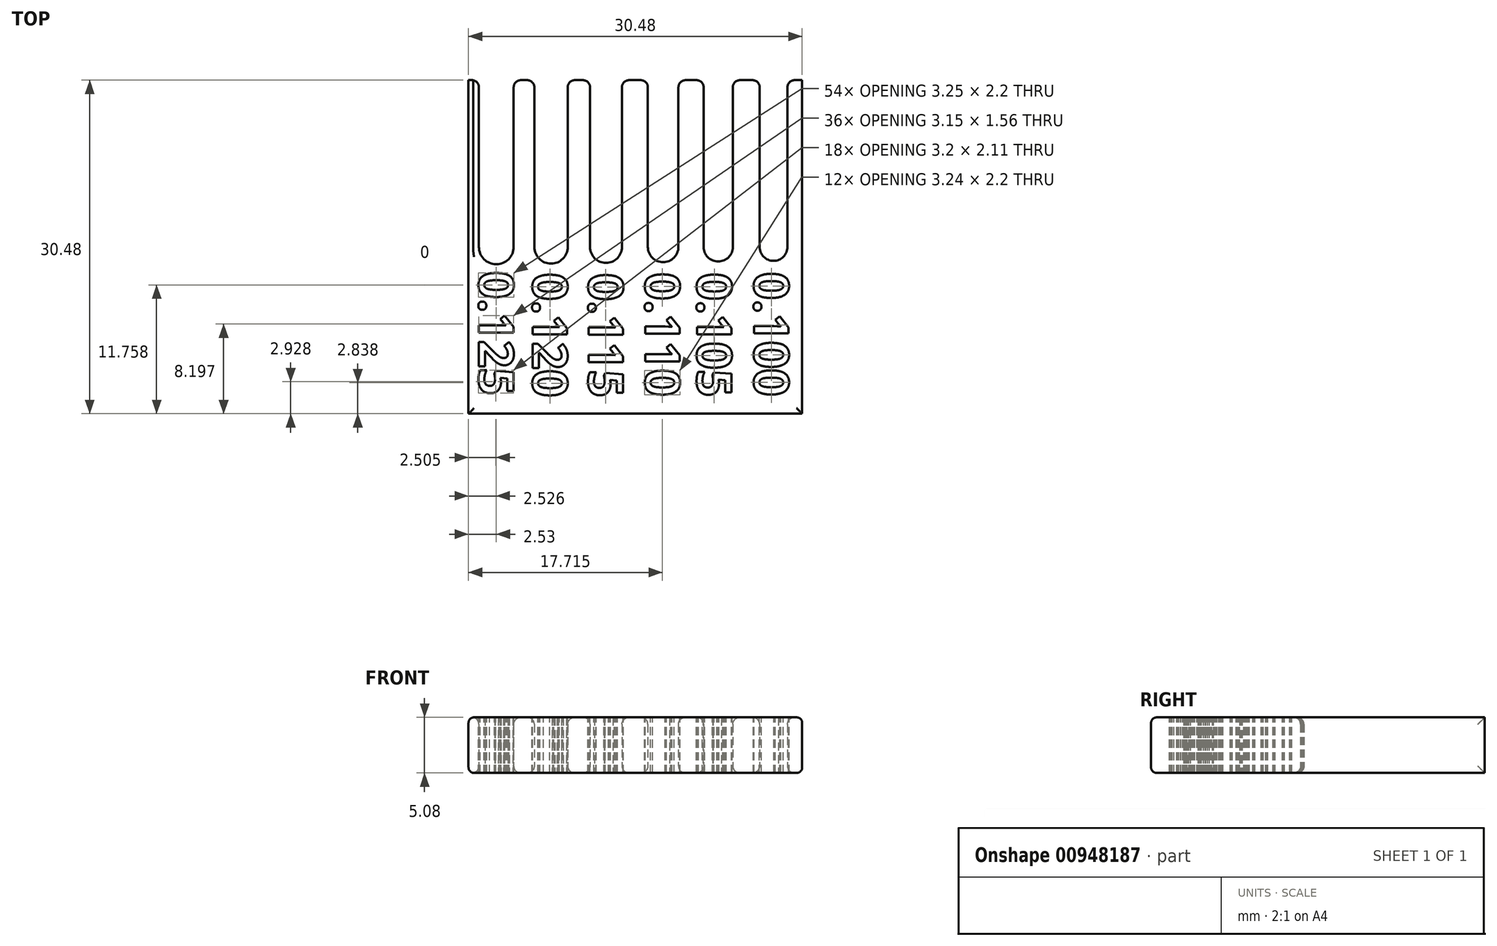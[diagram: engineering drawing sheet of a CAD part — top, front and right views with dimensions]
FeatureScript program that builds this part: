
annotation { "Feature Type Name" : "Feature", "Feature Type Description" : "" }
export const myFeature = defineFeature(function(context is Context, id is Id, definition is map)
    precondition{}
    {
        {
            var Q0;
            Q0=qCreatedBy(makeId("Top.planeOp"),FACE);
            var sketch = newSketch(context, id + "F0", { "sketchPlane" : qUnion([Q0])});
            skLineSegment(sketch, "E0.bottom", {"start": v(2.54, 15.24) * mm, "end": v(-2.54, 15.24) * mm});
            skLineSegment(sketch, "E0.top", {"start": v(2.54, -15.24) * mm, "end": v(-2.54, -15.24) * mm});
            skLineSegment(sketch, "E0.left", {"start": v(2.54, 15.24) * mm, "end": v(2.54, -15.24) * mm});
            skLineSegment(sketch, "E0.right", {"start": v(-2.54, 15.24) * mm, "end": v(-2.54, -15.24) * mm});
            skPoint(sketch, "E0.middle", {"position": v(0, 0) * mm});
            skLineSegment(sketch, "E1", {"start": v(-1.59, 15.24) * mm, "end": v(-1.59, 0) * mm});
            skArc(sketch, "E2", {"start": v(-1.59, 0) * mm, "mid": v(0, -1.59) * mm, "end": v(1.59, 0) * mm});
            skLineSegment(sketch, "E3", {"start": v(1.59, 0) * mm, "end": v(1.59, 15.24) * mm});
            skLineSegment(sketch, "E4.1.0.0", {"start": v(7.62, 15.24) * mm, "end": v(7.62, -15.24) * mm});
            skLineSegment(sketch, "E4.1.0.1", {"start": v(7.62, 15.24) * mm, "end": v(2.54, 15.24) * mm});
            skLineSegment(sketch, "E4.1.0.2", {"start": v(7.62, -15.24) * mm, "end": v(2.54, -15.24) * mm});
            skLineSegment(sketch, "E4.2.0.0", {"start": v(12.7, 15.24) * mm, "end": v(12.7, -15.24) * mm});
            skLineSegment(sketch, "E4.2.0.1", {"start": v(12.7, 15.24) * mm, "end": v(7.62, 15.24) * mm});
            skLineSegment(sketch, "E4.2.0.2", {"start": v(12.7, -15.24) * mm, "end": v(7.62, -15.24) * mm});
            skLineSegment(sketch, "E4.2.0.3", {"start": v(7.62, 15.24) * mm, "end": v(7.62, -15.24) * mm});
            skLineSegment(sketch, "E4.direction1", {"start": v(2.54, -15.24) * mm, "end": v(7.62, -15.24) * mm, "construction": true});
            skPoint(sketch, "E5.middle", {"position": v(5, 0) * mm});
            skLineSegment(sketch, "E6", {"start": v(3.47, 15.24) * mm, "end": v(3.47, 0) * mm});
            skArc(sketch, "E7", {"start": v(3.47, 0) * mm, "mid": v(5, -1.52) * mm, "end": v(6.52, 0) * mm});
            skLineSegment(sketch, "E8", {"start": v(6.52, 0) * mm, "end": v(6.52, 15.24) * mm});
            skPoint(sketch, "E9.middle", {"position": v(10.02, 0) * mm});
            skLineSegment(sketch, "E10", {"start": v(8.56, 15.24) * mm, "end": v(8.56, 0) * mm});
            skArc(sketch, "E11", {"start": v(8.56, 0) * mm, "mid": v(10.02, -1.46) * mm, "end": v(11.48, 0) * mm});
            skLineSegment(sketch, "E12", {"start": v(11.48, 0) * mm, "end": v(11.48, 15.24) * mm});
            skLineSegment(sketch, "E13.bottom", {"start": v(17.78, 15.24) * mm, "end": v(12.7, 15.24) * mm});
            skLineSegment(sketch, "E13.top", {"start": v(17.78, -15.24) * mm, "end": v(12.7, -15.24) * mm});
            skLineSegment(sketch, "E13.left", {"start": v(17.78, 15.24) * mm, "end": v(17.78, -15.24) * mm});
            skPoint(sketch, "E13.middle", {"position": v(15.24, 0) * mm});
            skLineSegment(sketch, "E14", {"start": v(13.84, 15.24) * mm, "end": v(13.84, 0) * mm});
            skArc(sketch, "E15", {"start": v(13.84, 0) * mm, "mid": v(15.24, -1.4) * mm, "end": v(16.64, 0) * mm});
            skLineSegment(sketch, "E16", {"start": v(16.64, 0) * mm, "end": v(16.64, 15.24) * mm});
            skLineSegment(sketch, "E17.1.0.0", {"start": v(22.86, 15.24) * mm, "end": v(22.86, -15.24) * mm});
            skLineSegment(sketch, "E17.1.0.1", {"start": v(22.86, 15.24) * mm, "end": v(17.78, 15.24) * mm});
            skLineSegment(sketch, "E17.1.0.2", {"start": v(22.86, -15.24) * mm, "end": v(17.78, -15.24) * mm});
            skLineSegment(sketch, "E17.2.0.0", {"start": v(27.94, 15.24) * mm, "end": v(27.94, -15.24) * mm});
            skLineSegment(sketch, "E17.2.0.1", {"start": v(27.94, 15.24) * mm, "end": v(22.86, 15.24) * mm});
            skLineSegment(sketch, "E17.2.0.2", {"start": v(27.94, -15.24) * mm, "end": v(22.86, -15.24) * mm});
            skLineSegment(sketch, "E17.2.0.3", {"start": v(22.86, 15.24) * mm, "end": v(22.86, -15.24) * mm});
            skLineSegment(sketch, "E17.direction1", {"start": v(17.78, -15.24) * mm, "end": v(22.86, -15.24) * mm, "construction": true});
            skPoint(sketch, "E18.middle", {"position": v(20.27, 0) * mm});
            skLineSegment(sketch, "E19", {"start": v(18.94, 15.24) * mm, "end": v(18.94, 0) * mm});
            skArc(sketch, "E20", {"start": v(18.94, 0) * mm, "mid": v(20.27, -1.33) * mm, "end": v(21.6, 0) * mm});
            skLineSegment(sketch, "E21", {"start": v(21.6, 0) * mm, "end": v(21.6, 15.24) * mm});
            skPoint(sketch, "E22.middle", {"position": v(25.32, 0) * mm});
            skLineSegment(sketch, "E23", {"start": v(24.05, 15.24) * mm, "end": v(24.05, 0) * mm});
            skArc(sketch, "E24", {"start": v(24.05, 0) * mm, "mid": v(25.32, -1.27) * mm, "end": v(26.6, 0) * mm});
            skLineSegment(sketch, "E25", {"start": v(26.6, 0) * mm, "end": v(26.6, 15.24) * mm});
            skSolve(sketch);
        }
        {
            var Q0;
            Q0=makeQuery(id+"F0.imprint","IMPRINT",FACE,{"disambiguationData":[TD([[makeQuery(id+"F0.imprint","IMPRINT",EDGE,{"derivedFrom":sQuery(id+"F0.wireOp",EDGE,"E0.top")}),-1.0]])]});
            var Q1;
            Q1=makeQuery(id+"F0.imprint","IMPRINT",FACE,{"disambiguationData":[TD([[makeQuery(id+"F0.imprint","IMPRINT",EDGE,{"derivedFrom":sQuery(id+"F0.wireOp",EDGE,"E4.1.0.2")}),-1.0]])]});
            var Q2;
            Q2=makeQuery(id+"F0.imprint","IMPRINT",FACE,{"disambiguationData":[TD([[makeQuery(id+"F0.imprint","IMPRINT",EDGE,{"derivedFrom":sQuery(id+"F0.wireOp",EDGE,"E4.2.0.2")}),-1.0]])]});
            var Q3;
            Q3=makeQuery(id+"F0.imprint","IMPRINT",FACE,{"disambiguationData":[TD([[makeQuery(id+"F0.imprint","IMPRINT",EDGE,{"derivedFrom":sQuery(id+"F0.wireOp",EDGE,"E13.top")}),-1.0]])]});
            var Q4;
            Q4=makeQuery(id+"F0.imprint","IMPRINT",FACE,{"disambiguationData":[TD([[makeQuery(id+"F0.imprint","IMPRINT",EDGE,{"derivedFrom":sQuery(id+"F0.wireOp",EDGE,"E17.1.0.2")}),-1.0]])]});
            var Q5;
            {var subQ3=sQuery(id+"F0.wireOp",EDGE,"E17.2.0.0");Q5=makeQuery(id+"F0.imprint","IMPRINT",FACE,{"disambiguationData":[TD([[makeQuery(id+"F0.imprint","IMPRINT",EDGE,{"derivedFrom":subQ3}),-1.0]])]});}
            extrude(context, id + "F1", {"entities" : qUnion([Q0, Q1, Q2, Q3, Q4, Q5]), "depth" : 5.08 * mm, "offsetDistance" : 25.4 * mm});
        }
        {
            var Q0;
            Q0=makeQuery(id+"F1.opExtrude","CAP_EDGE",EDGE,{"disambiguationData":[OSD([sQuery(id+"F0.wireOp",EDGE,"E2")])],"isStart":false});
            var Q1;
            Q1=makeQuery(id+"F1.opExtrude","CAP_EDGE",EDGE,{"disambiguationData":[OSD([sQuery(id+"F0.wireOp",EDGE,"E7")])],"isStart":false});
            var Q2;
            Q2=makeQuery(id+"F1.opExtrude","CAP_EDGE",EDGE,{"disambiguationData":[OSD([sQuery(id+"F0.wireOp",EDGE,"E11")])],"isStart":false});
            var Q3;
            Q3=makeQuery(id+"F1.opExtrude","CAP_EDGE",EDGE,{"disambiguationData":[OSD([sQuery(id+"F0.wireOp",EDGE,"E15")])],"isStart":false});
            var Q4;
            Q4=makeQuery(id+"F1.opExtrude","CAP_EDGE",EDGE,{"disambiguationData":[OSD([sQuery(id+"F0.wireOp",EDGE,"E20")])],"isStart":false});
            var Q5;
            Q5=makeQuery(id+"F1.opExtrude","CAP_EDGE",EDGE,{"disambiguationData":[OSD([sQuery(id+"F0.wireOp",EDGE,"E24")])],"isStart":false});
            var Q6;
            Q6=makeQuery(id+"F1.opExtrude","CAP_EDGE",EDGE,{"disambiguationData":[OSD([sQuery(id+"F0.wireOp",EDGE,"E24")])],"isStart":true});
            var Q7;
            Q7=makeQuery(id+"F1.opExtrude","CAP_EDGE",EDGE,{"disambiguationData":[OSD([sQuery(id+"F0.wireOp",EDGE,"E20")])],"isStart":true});
            var Q8;
            Q8=makeQuery(id+"F1.opExtrude","CAP_EDGE",EDGE,{"disambiguationData":[OSD([sQuery(id+"F0.wireOp",EDGE,"E15")])],"isStart":true});
            var Q9;
            Q9=makeQuery(id+"F1.opExtrude","CAP_EDGE",EDGE,{"disambiguationData":[OSD([sQuery(id+"F0.wireOp",EDGE,"E11")])],"isStart":true});
            var Q10;
            Q10=makeQuery(id+"F1.opExtrude","CAP_EDGE",EDGE,{"disambiguationData":[OSD([sQuery(id+"F0.wireOp",EDGE,"E7")])],"isStart":true});
            var Q11;
            Q11=makeQuery(id+"F1.opExtrude","CAP_EDGE",EDGE,{"disambiguationData":[OSD([sQuery(id+"F0.wireOp",EDGE,"E2")])],"isStart":true});
            var Q12;
            Q12=makeQuery(id+"F1.opExtrude","SWEPT_EDGE",EDGE,{"disambiguationData":[OSD([sQuery(id+"F0.wireOp",EDGE,"E17.2.0.1"),sQuery(id+"F0.wireOp",EDGE,"E23")])]});
            var Q13;
            Q13=makeQuery(id+"F1.opExtrude","SWEPT_EDGE",EDGE,{"disambiguationData":[OSD([sQuery(id+"F0.wireOp",EDGE,"E17.2.0.1"),sQuery(id+"F0.wireOp",EDGE,"E25")])]});
            var Q14;
            Q14=makeQuery(id+"F1.opExtrude","SWEPT_EDGE",EDGE,{"disambiguationData":[OSD([sQuery(id+"F0.wireOp",EDGE,"E17.1.0.1"),sQuery(id+"F0.wireOp",EDGE,"E21")])]});
            var Q15;
            Q15=makeQuery(id+"F1.opExtrude","SWEPT_EDGE",EDGE,{"disambiguationData":[OSD([sQuery(id+"F0.wireOp",EDGE,"E17.1.0.1"),sQuery(id+"F0.wireOp",EDGE,"E19")])]});
            var Q16;
            Q16=makeQuery(id+"F1.opExtrude","SWEPT_EDGE",EDGE,{"disambiguationData":[OSD([sQuery(id+"F0.wireOp",EDGE,"E13.bottom"),sQuery(id+"F0.wireOp",EDGE,"E14")])]});
            var Q17;
            Q17=makeQuery(id+"F1.opExtrude","SWEPT_EDGE",EDGE,{"disambiguationData":[OSD([sQuery(id+"F0.wireOp",EDGE,"E4.2.0.1"),sQuery(id+"F0.wireOp",EDGE,"E10")])]});
            var Q18;
            Q18=makeQuery(id+"F1.opExtrude","SWEPT_EDGE",EDGE,{"disambiguationData":[OSD([sQuery(id+"F0.wireOp",EDGE,"E4.1.0.1"),sQuery(id+"F0.wireOp",EDGE,"E6")])]});
            var Q19;
            Q19=makeQuery(id+"F1.opExtrude","SWEPT_EDGE",EDGE,{"disambiguationData":[OSD([sQuery(id+"F0.wireOp",EDGE,"E0.bottom"),sQuery(id+"F0.wireOp",EDGE,"E1")])]});
            var Q20;
            Q20=makeQuery(id+"F1.opExtrude","SWEPT_EDGE",EDGE,{"disambiguationData":[OSD([sQuery(id+"F0.wireOp",EDGE,"E13.bottom"),sQuery(id+"F0.wireOp",EDGE,"E16")])]});
            var Q21;
            Q21=makeQuery(id+"F1.opExtrude","SWEPT_EDGE",EDGE,{"disambiguationData":[OSD([sQuery(id+"F0.wireOp",EDGE,"E4.2.0.1"),sQuery(id+"F0.wireOp",EDGE,"E12")])]});
            var Q22;
            Q22=makeQuery(id+"F1.opExtrude","SWEPT_EDGE",EDGE,{"disambiguationData":[OSD([sQuery(id+"F0.wireOp",EDGE,"E4.1.0.1"),sQuery(id+"F0.wireOp",EDGE,"E8")])]});
            var Q23;
            Q23=makeQuery(id+"F1.opExtrude","SWEPT_EDGE",EDGE,{"disambiguationData":[OSD([sQuery(id+"F0.wireOp",EDGE,"E0.bottom"),sQuery(id+"F0.wireOp",EDGE,"E3")])]});
            fillet(context, id + "F2", {"entities" : qUnion([Q0, Q1, Q2, Q3, Q4, Q5, Q6, Q7, Q8, Q9, Q10, Q11, Q12, Q13, Q14, Q15, Q16, Q17, Q18, Q19, Q20, Q21, Q22, Q23]), "radius" : 0.64 * mm, "tangentPropagation" : true, "allowEdgeOverflow" : false});
        }
        {
            var Q0;
            Q0=makeQuery(id+"F1.opExtrude","CAP_EDGE",EDGE,{"disambiguationData":[OSD([sQuery(id+"F0.wireOp",EDGE,"E17.2.0.0")])],"isStart":false});
            var Q1;
            Q1=makeQuery(id+"F1.opExtrude","CAP_EDGE",EDGE,{"disambiguationData":[OSD([sQuery(id+"F0.wireOp",EDGE,"E0.top"),sQuery(id+"F0.wireOp",EDGE,"E4.1.0.2"),sQuery(id+"F0.wireOp",EDGE,"E4.2.0.2"),sQuery(id+"F0.wireOp",EDGE,"E13.top"),sQuery(id+"F0.wireOp",EDGE,"E17.1.0.2"),sQuery(id+"F0.wireOp",EDGE,"E17.2.0.2")])],"isStart":false});
            var Q2;
            Q2=makeQuery(id+"F1.opExtrude","CAP_EDGE",EDGE,{"disambiguationData":[OSD([sQuery(id+"F0.wireOp",EDGE,"E0.right")])],"isStart":false});
            var Q3;
            Q3=makeQuery(id+"F1.opExtrude","CAP_EDGE",EDGE,{"disambiguationData":[OSD([sQuery(id+"F0.wireOp",EDGE,"E17.2.0.0")])],"isStart":true});
            var Q4;
            Q4=makeQuery(id+"F1.opExtrude","CAP_EDGE",EDGE,{"disambiguationData":[OSD([sQuery(id+"F0.wireOp",EDGE,"E0.top"),sQuery(id+"F0.wireOp",EDGE,"E4.1.0.2"),sQuery(id+"F0.wireOp",EDGE,"E4.2.0.2"),sQuery(id+"F0.wireOp",EDGE,"E13.top"),sQuery(id+"F0.wireOp",EDGE,"E17.1.0.2"),sQuery(id+"F0.wireOp",EDGE,"E17.2.0.2")])],"isStart":true});
            var Q5;
            Q5=makeQuery(id+"F1.opExtrude","CAP_EDGE",EDGE,{"disambiguationData":[OSD([sQuery(id+"F0.wireOp",EDGE,"E0.right")])],"isStart":true});
            fillet(context, id + "F3", {"entities" : qUnion([Q0, Q1, Q2, Q3, Q4, Q5]), "radius" : 0.5 * mm, "tangentPropagation" : true, "allowEdgeOverflow" : false});
        }
        {
            var Q0;
            Q0=makeQuery(id+"F1.opExtrude","CAP_FACE",FACE,{"disambiguationData":[OSD([sQuery(id+"F0.wireOp",EDGE,"E0.bottom"),sQuery(id+"F0.wireOp",EDGE,"E0.top"),sQuery(id+"F0.wireOp",EDGE,"E0.right"),sQuery(id+"F0.wireOp",EDGE,"E1"),sQuery(id+"F0.wireOp",EDGE,"E2"),sQuery(id+"F0.wireOp",EDGE,"E3"),sQuery(id+"F0.wireOp",EDGE,"E4.1.0.1"),sQuery(id+"F0.wireOp",EDGE,"E4.1.0.2"),sQuery(id+"F0.wireOp",EDGE,"E4.2.0.1"),sQuery(id+"F0.wireOp",EDGE,"E4.2.0.2"),sQuery(id+"F0.wireOp",EDGE,"E6"),sQuery(id+"F0.wireOp",EDGE,"E7"),sQuery(id+"F0.wireOp",EDGE,"E8"),sQuery(id+"F0.wireOp",EDGE,"E10"),sQuery(id+"F0.wireOp",EDGE,"E11"),sQuery(id+"F0.wireOp",EDGE,"E12"),sQuery(id+"F0.wireOp",EDGE,"E13.bottom"),sQuery(id+"F0.wireOp",EDGE,"E13.top"),sQuery(id+"F0.wireOp",EDGE,"E14"),sQuery(id+"F0.wireOp",EDGE,"E15"),sQuery(id+"F0.wireOp",EDGE,"E16"),sQuery(id+"F0.wireOp",EDGE,"E17.1.0.1"),sQuery(id+"F0.wireOp",EDGE,"E17.1.0.2"),sQuery(id+"F0.wireOp",EDGE,"E17.2.0.0"),sQuery(id+"F0.wireOp",EDGE,"E17.2.0.1"),sQuery(id+"F0.wireOp",EDGE,"E17.2.0.2"),sQuery(id+"F0.wireOp",EDGE,"E19"),sQuery(id+"F0.wireOp",EDGE,"E20"),sQuery(id+"F0.wireOp",EDGE,"E21"),sQuery(id+"F0.wireOp",EDGE,"E23"),sQuery(id+"F0.wireOp",EDGE,"E24"),sQuery(id+"F0.wireOp",EDGE,"E25")])],"isStart":false});
            var sketch = newSketch(context, id + "F4", { "sketchPlane" : qUnion([Q0])});
            skText(sketch, "E26", { "text": "0.125\n", "fontName": "OpenSans-Bold.ttf"});
            skText(sketch, "E27", { "text": "0.120\n\n", "fontName": "OpenSans-Bold.ttf"});
            skText(sketch, "E28", { "text": "0.115\n\n", "fontName": "OpenSans-Bold.ttf"});
            skText(sketch, "E29", { "text": "0.110\n\n", "fontName": "OpenSans-Bold.ttf"});
            skText(sketch, "E30", { "text": "0.105\n", "fontName": "OpenSans-Bold.ttf"});
            skText(sketch, "E31", { "text": "0.100", "fontName": "OpenSans-Bold.ttf"});
            const initialGuessF4  = {"E26": [-0.00159, -0.00222, 0, -1, 0.00318], "E27": [0.00332, -0.00238, 0, -1, 0.00318], "E28": [0.00842, -0.00241, 0, -1, 0.00318], "E29": [0.0136, -0.00235, 0, -1, 0.00317], "E30": [0.01833, -0.00237, 0, -1, 0.00318], "E31": [0.02354, -0.0023, 0, -1, 0.00318]};
            skSetInitialGuess(sketch, initialGuessF4);
            skSolve(sketch);
        }
        {
            var Q0;
            Q0 = qSketchRegion(id + "F4", true);
            extrude(context, id + "F5", {"entities" : qUnion([Q0]), "operationType" : NewBodyOperationType.REMOVE, "oppositeDirection" : true, "depth" : 25.4 * mm, "offsetDistance" : 25.4 * mm});
        }
    });
